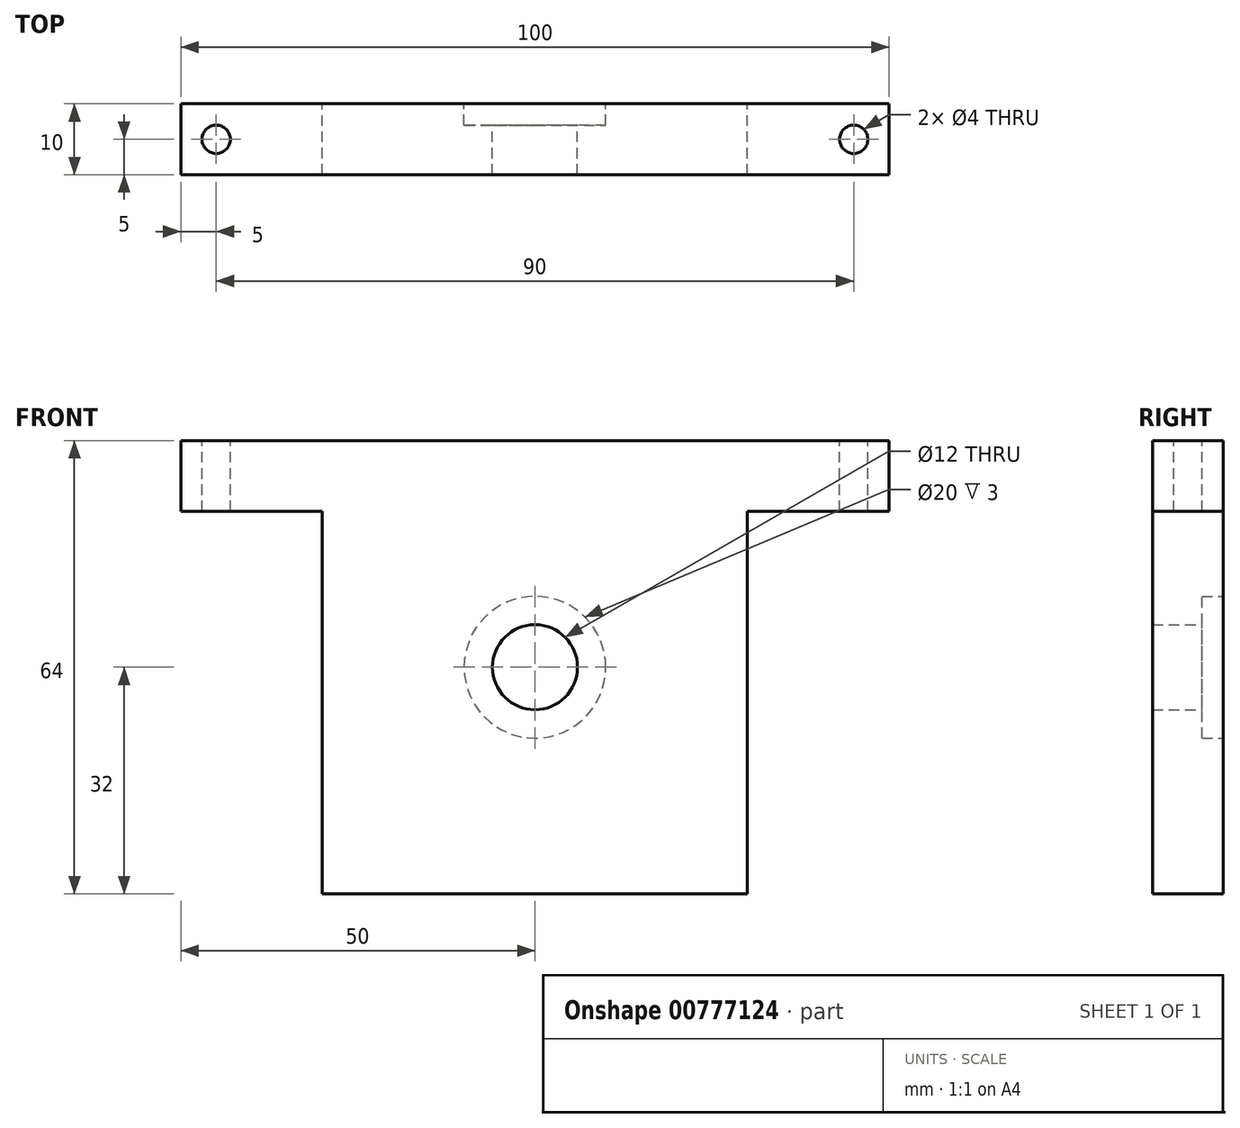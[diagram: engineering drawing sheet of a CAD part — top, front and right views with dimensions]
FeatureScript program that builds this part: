
annotation { "Feature Type Name" : "Feature", "Feature Type Description" : "" }
export const myFeature = defineFeature(function(context is Context, id is Id, definition is map)
    precondition{}
    {
        {
            var Q0;
            Q0=qCreatedBy(makeId("Front.planeOp"),FACE);
            var sketch = newSketch(context, id + "F0", { "sketchPlane" : qUnion([Q0])});
            skLineSegment(sketch, "E0.bottom", {"start": v(-100, 64) * mm, "end": v(0, 64) * mm});
            skLineSegment(sketch, "E0.top", {"start": v(-100, 0) * mm, "end": v(0, 0) * mm});
            skLineSegment(sketch, "E0.left", {"start": v(-100, 64) * mm, "end": v(-100, 0) * mm});
            skLineSegment(sketch, "E0.right", {"start": v(0, 64) * mm, "end": v(0, 0) * mm});
            skLineSegment(sketch, "E1.bottom", {"start": v(-100, 0) * mm, "end": v(-80, 0) * mm});
            skLineSegment(sketch, "E1.top", {"start": v(-100, 54) * mm, "end": v(-80, 54) * mm});
            skLineSegment(sketch, "E1.left", {"start": v(-100, 0) * mm, "end": v(-100, 54) * mm});
            skLineSegment(sketch, "E1.right", {"start": v(-80, 0) * mm, "end": v(-80, 54) * mm});
            skLineSegment(sketch, "E2.bottom", {"start": v(0, 0) * mm, "end": v(-20, 0) * mm});
            skLineSegment(sketch, "E2.top", {"start": v(0, 54) * mm, "end": v(-20, 54) * mm});
            skLineSegment(sketch, "E2.left", {"start": v(0, 0) * mm, "end": v(0, 54) * mm});
            skLineSegment(sketch, "E2.right", {"start": v(-20, 0) * mm, "end": v(-20, 54) * mm});
            skCircle(sketch, "E3", {"center": v(-50, 32) * mm, "radius": 6 * mm});
            skPoint(sketch, "E3.centerSnap0", {"position": v(-100, 32) * mm});
            skPoint(sketch, "E3.centerSnap1", {"position": v(-50, 64) * mm});
            skCircle(sketch, "E4", {"center": v(-50, 32) * mm, "radius": 10 * mm});
            skSolve(sketch);
        }
        {
            var Q0;
            Q0=makeQuery(id+"F0.imprint","IMPRINT",FACE,{"disambiguationData":[TD([[makeQuery(id+"F0.imprint","IMPRINT",EDGE,{"derivedFrom":sQuery(id+"F0.wireOp",EDGE,"E0.bottom")}),-1.0]])]});
            var Q1;
            Q1=makeQuery(id+"F0.imprint","IMPRINT",FACE,{"disambiguationData":[TD([[makeQuery(id+"F0.imprint","IMPRINT",EDGE,{"derivedFrom":sQuery(id+"F0.wireOp",EDGE,"E3")}),-1.0]])]});
            extrude(context, id + "F1", {"entities" : qUnion([Q0, Q1]), "depth" : 10 * mm, "offsetDistance" : 25 * mm});
        }
        {
            var Q0;
            Q0=makeQuery(id+"F1.opExtrude","SWEPT_FACE",FACE,{"disambiguationData":[OSD([sQuery(id+"F0.wireOp",EDGE,"E0.bottom")])]});
            var sketch = newSketch(context, id + "F2", { "sketchPlane" : qUnion([Q0])});
            skCircle(sketch, "E5", {"center": v(-95, -5) * mm, "radius": 2 * mm});
            skCircle(sketch, "E6", {"center": v(-5, -5) * mm, "radius": 2 * mm});
            skSolve(sketch);
        }
        {
            var Q0;
            Q0=makeQuery(id+"F2.imprint","IMPRINT",FACE,{"disambiguationData":[TD([[makeQuery(id+"F2.imprint","IMPRINT",EDGE,{"derivedFrom":sQuery(id+"F2.wireOp",EDGE,"E5")}),1.0]])]});
            var Q1;
            Q1=makeQuery(id+"F2.imprint","IMPRINT",FACE,{"disambiguationData":[TD([[makeQuery(id+"F2.imprint","IMPRINT",EDGE,{"derivedFrom":sQuery(id+"F2.wireOp",EDGE,"E6")}),1.0]])]});
            extrude(context, id + "F3", {"entities" : qUnion([Q0, Q1]), "operationType" : NewBodyOperationType.REMOVE, "endBound" : BoundingType.THROUGH_ALL, "oppositeDirection" : true, "depth" : 25 * mm, "offsetDistance" : 25 * mm});
        }
        {
            var Q0;
            Q0=makeQuery(id+"F0.imprint","IMPRINT",FACE,{"disambiguationData":[TD([[makeQuery(id+"F0.imprint","IMPRINT",EDGE,{"derivedFrom":sQuery(id+"F0.wireOp",EDGE,"E3")}),-1.0]])]});
            extrude(context, id + "F4", {"entities" : qUnion([Q0]), "operationType" : NewBodyOperationType.REMOVE, "depth" : 3 * mm, "offsetDistance" : 25 * mm});
        }
    });
